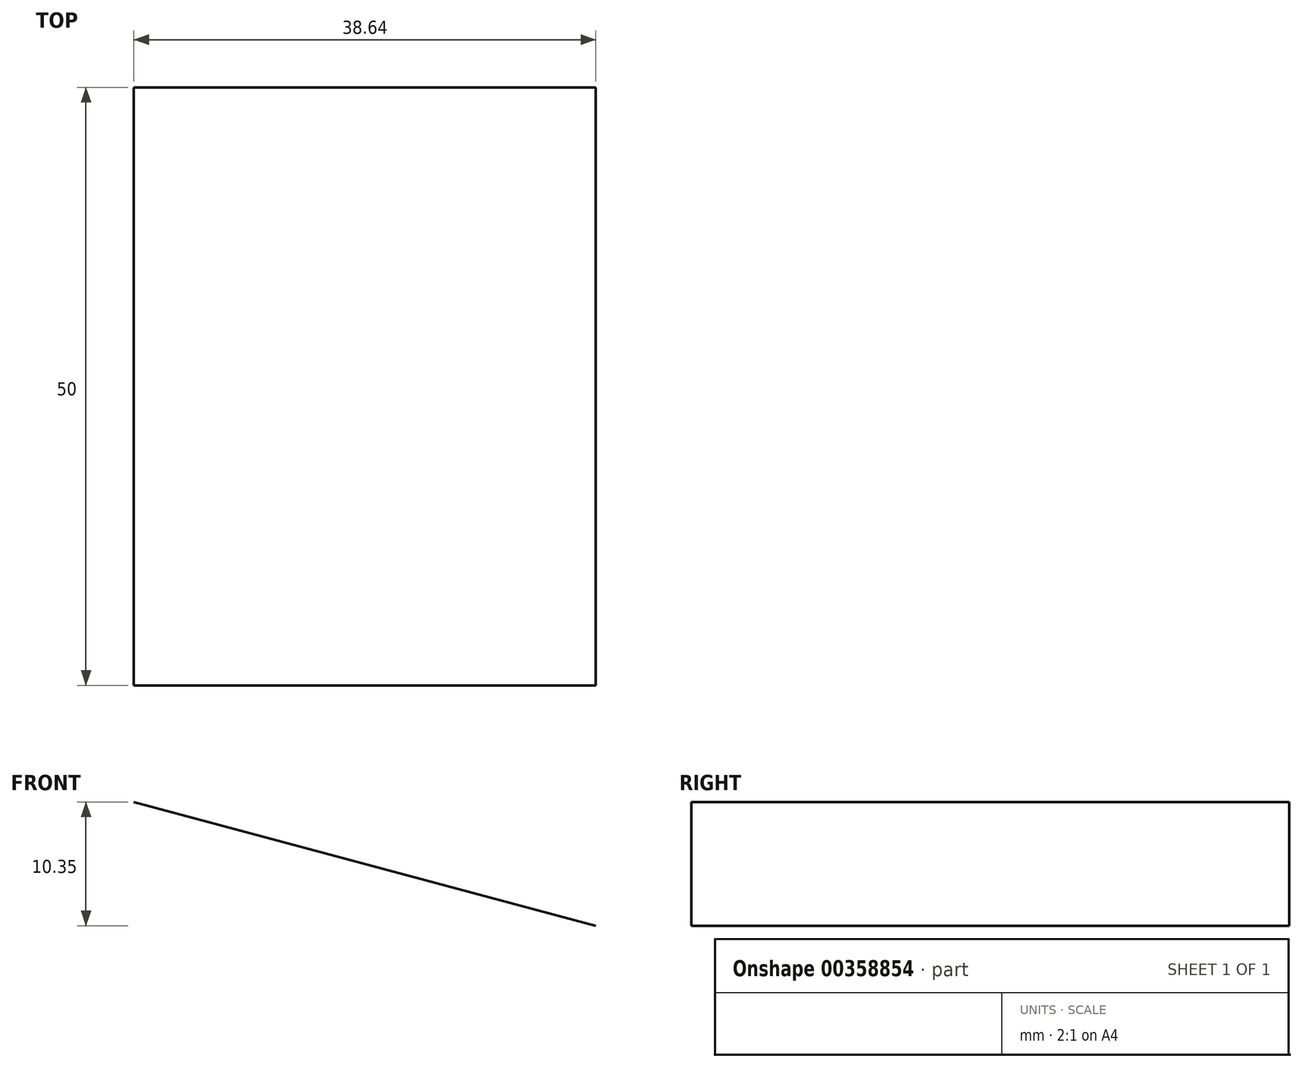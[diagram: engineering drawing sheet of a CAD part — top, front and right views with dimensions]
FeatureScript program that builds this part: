
annotation { "Feature Type Name" : "Feature", "Feature Type Description" : "" }
export const myFeature = defineFeature(function(context is Context, id is Id, definition is map)
    precondition{}
    {
        {
            var Q0;
            Q0=qCreatedBy(makeId("Right.planeOp"),FACE);
            var sketch = newSketch(context, id + "F0", { "sketchPlane" : qUnion([Q0])});
            skLineSegment(sketch, "E0", {"start": v(0, 0) * mm, "end": v(-20, 0) * mm});
            skLineSegment(sketch, "E1", {"start": v(-20, 0) * mm, "end": v(-15.96, 11.1) * mm});
            skLineSegment(sketch, "E2", {"start": v(-11.26, 14.4) * mm, "end": v(0, 14.4) * mm});
            skPoint(sketch, "E3.visualSharp", {"position": v(-14.76, 14.4) * mm});
            skArc(sketch, "E3.filletArc", {"start": v(-11.26, 14.4) * mm, "mid": v(-14.13, 13.5) * mm, "end": v(-15.96, 11.1) * mm});
            skLineSegment(sketch, "E4.MirrorCS", {"start": v(0, 0) * mm, "end": v(20, 0) * mm});
            skLineSegment(sketch, "E5.MirrorCS", {"start": v(11.26, 14.4) * mm, "end": v(0, 14.4) * mm});
            skLineSegment(sketch, "E6.MirrorCS", {"start": v(20, 0) * mm, "end": v(15.96, 11.1) * mm});
            skArc(sketch, "E7.MirrorCS", {"start": v(11.26, 14.4) * mm, "mid": v(14.13, 13.5) * mm, "end": v(15.96, 11.1) * mm});
            skSolve(sketch);
        }
        {
            var Q0;
            Q0=qCreatedBy(makeId("Front.planeOp"),FACE);
            var sketch = newSketch(context, id + "F1", { "sketchPlane" : qUnion([Q0])});
            skLineSegment(sketch, "E8", {"start": v(0, 0) * mm, "end": v(43.55, 0) * mm, "construction": true});
            skLineSegment(sketch, "E9", {"start": v(0, 0) * mm, "end": v(38.64, -10.35) * mm});
            skPoint(sketch, "E10.1.internal.snap0", {"position": v(21.78, 0) * mm});
            skSolve(sketch);
        }
        {
            var Q0;
            Q0=qCreatedBy(makeId("Front.planeOp"),FACE);
            var sketch = newSketch(context, id + "F2", { "sketchPlane" : qUnion([Q0])});
            skFitSpline(sketch, "E11", {"points": [v(0, 0) * mm, v(17.5, -3.07) * mm, v(32.93, -8.82) * mm], "startDerivative": vector(40.18, -4.82) * mm, "endDerivative": vector(36.54, -16.44) * mm});
            skSolve(sketch);
        }
        {
            var Q0;
            Q0=qCreatedBy(makeId("Front.planeOp"),FACE);
            var sketch = newSketch(context, id + "F3", { "sketchPlane" : qUnion([Q0])});
            skPoint(sketch, "E12.0", {"position": v(0, 14.4) * mm});
            skPoint(sketch, "E12.1", {"position": v(32.93, -8.82) * mm});
            skFitSpline(sketch, "E13", {"points": [v(0, 14.4) * mm, v(22.3, 6.74) * mm, v(32.93, -8.82) * mm], "startDerivative": vector(47.16, 0.74) * mm, "endDerivative": vector(11.65, -47.3) * mm});
            skSolve(sketch);
        }
        {
            var Q0;
            Q0=sQuery(id+"F1.wireOp",EDGE,"E9");
            extrude(context, id + "F4", {"bodyType" : ToolBodyType.SURFACE, "surfaceEntities" : qUnion([Q0]), "depth" : 25 * mm, "hasSecondDirection" : true, "secondDirectionOppositeDirection" : true, "secondDirectionDepth" : 25 * mm});
        }
    });
